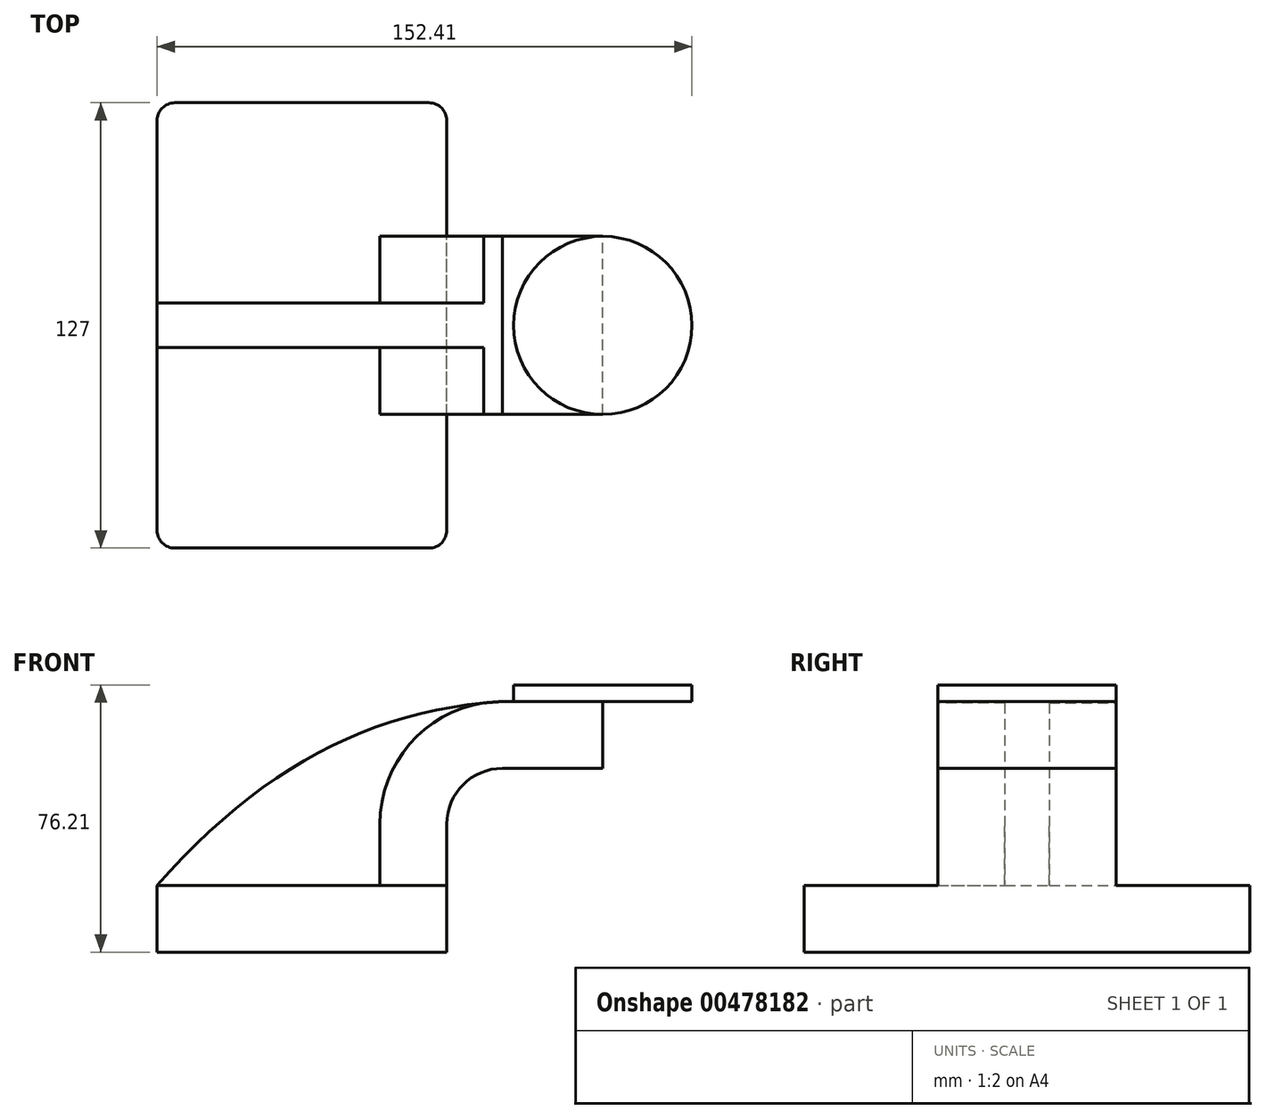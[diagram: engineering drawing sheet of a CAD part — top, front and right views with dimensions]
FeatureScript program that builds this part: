
annotation { "Feature Type Name" : "Feature", "Feature Type Description" : "" }
export const myFeature = defineFeature(function(context is Context, id is Id, definition is map)
    precondition{}
    {
        {
            var Q0;
            Q0=qCreatedBy(makeId("Front.planeOp"),FACE);
            var sketch = newSketch(context, id + "F0", { "sketchPlane" : qUnion([Q0])});
            skLineSegment(sketch, "E0.bottom", {"start": v(41.28, -9.52) * mm, "end": v(-41.27, -9.52) * mm});
            skLineSegment(sketch, "E0.top", {"start": v(41.27, 9.53) * mm, "end": v(-41.27, 9.53) * mm});
            skLineSegment(sketch, "E0.left", {"start": v(41.28, -9.52) * mm, "end": v(41.28, 9.53) * mm});
            skLineSegment(sketch, "E0.right", {"start": v(-41.27, -9.52) * mm, "end": v(-41.27, 9.53) * mm});
            skPoint(sketch, "E0.middle", {"position": v(0, 0) * mm});
            skLineSegment(sketch, "E1", {"start": v(41.27, 9.53) * mm, "end": v(41.27, 27) * mm});
            skArc(sketch, "E2", {"start": v(41.28, 27) * mm, "mid": v(45.92, 38.23) * mm, "end": v(57.15, 42.88) * mm});
            skLineSegment(sketch, "E3", {"start": v(57.15, 42.88) * mm, "end": v(85.72, 42.88) * mm});
            skLineSegment(sketch, "E4.bottom", {"start": v(111.12, 66.68) * mm, "end": v(60.32, 66.68) * mm});
            skLineSegment(sketch, "E4.top", {"start": v(111.12, 38.1) * mm, "end": v(60.32, 38.1) * mm});
            skLineSegment(sketch, "E4.left", {"start": v(111.12, 66.68) * mm, "end": v(111.12, 38.1) * mm});
            skLineSegment(sketch, "E4.right", {"start": v(60.32, 66.68) * mm, "end": v(60.32, 38.1) * mm});
            skPoint(sketch, "E4.middle", {"position": v(85.72, 52.39) * mm});
            skLineSegment(sketch, "E5", {"start": v(111.12, 66.68) * mm, "end": v(111.12, -9.67) * mm});
            skLineSegment(sketch, "E6.0", {"start": v(57.15, 61.93) * mm, "end": v(85.72, 61.93) * mm});
            skArc(sketch, "E6.1", {"start": v(22.23, 27) * mm, "mid": v(32.45, 51.7) * mm, "end": v(57.15, 61.93) * mm});
            skLineSegment(sketch, "E6.2", {"start": v(22.23, 9.53) * mm, "end": v(22.23, 27) * mm});
            skFitSpline(sketch, "E7", {"points": [v(57.15, 61.93) * mm, v(-41.28, 9.52) * mm], "startDerivative": vector(-112.77, -6.5) * mm, "endDerivative": vector(-88.55, -100.44) * mm});
            skLineSegment(sketch, "E8", {"start": v(85.72, 66.68) * mm, "end": v(85.72, 38.1) * mm});
            skSolve(sketch);
        }
        {
            var Q0;
            Q0=makeQuery(id+"F0.imprint","IMPRINT",FACE,{"disambiguationData":[TD([[makeQuery(id+"F0.imprint","IMPRINT",EDGE,{"derivedFrom":sQuery(id+"F0.wireOp",EDGE,"E0.bottom")}),-1.0]])]});
            extrude(context, id + "F1", {"entities" : qUnion([Q0]), "endBound" : BoundingType.SYMMETRIC, "depth" : 127 * mm});
        }
        {
            var Q0;
            {var subQ4=sQuery(id+"F0.wireOp",EDGE,"E1");Q0=makeQuery(id+"F0.imprint","IMPRINT",FACE,{"disambiguationData":[TD([[makeQuery(id+"F0.imprint","IMPRINT",EDGE,{"derivedFrom":subQ4}),1.0]])]});}
            var Q1;
            {var subQ0=sQuery(id+"F0.wireOp",EDGE,"E8");var subQ1=sQuery(id+"F0.wireOp",EDGE,"E3");var subQ2=makeQuery(id+"F0.imprint","INTERSECT",VERTEX,{"derivedFrom":[subQ1,subQ0]});Q1=makeQuery(id+"F0.imprint","IMPRINT",FACE,{"disambiguationData":[TD([[makeQuery(id+"F0.imprint","IMPRINT",EDGE,{"disambiguationData":[TD([[subQ2,1.0]])],"derivedFrom":subQ1}),1.0]])]});}
            extrude(context, id + "F2", {"entities" : qUnion([Q0, Q1]), "operationType" : NewBodyOperationType.ADD, "endBound" : BoundingType.SYMMETRIC, "depth" : 50.8 * mm});
        }
        {
            var Q0;
            {var subQ3=sQuery(id+"F0.wireOp",EDGE,"E6.2");Q0=makeQuery(id+"F0.imprint","IMPRINT",FACE,{"disambiguationData":[TD([[makeQuery(id+"F0.imprint","IMPRINT",EDGE,{"derivedFrom":subQ3}),1.0]])]});}
            extrude(context, id + "F3", {"entities" : qUnion([Q0]), "operationType" : NewBodyOperationType.ADD, "endBound" : BoundingType.SYMMETRIC, "depth" : 12.7 * mm});
        }
        {
            var Q0;
            {var subQ0=sQuery(id+"F0.wireOp",EDGE,"E5");var subQ1=sQuery(id+"F0.wireOp",EDGE,"E4.bottom");var subQ2=makeQuery(id+"F0.imprint","INTERSECT",VERTEX,{"derivedFrom":[subQ1,subQ0]});Q0=makeQuery(id+"F0.imprint","IMPRINT",FACE,{"disambiguationData":[TD([[makeQuery(id+"F0.imprint","IMPRINT",EDGE,{"disambiguationData":[TD([[subQ2,-1.0]])],"derivedFrom":subQ1}),1.0]])]});}
            var Q1;
            Q1=sQuery(id+"F0.wireOp",EDGE,"E8");
            revolve(context, id + "F4", {"operationType" : NewBodyOperationType.ADD, "entities" : qUnion([Q0]), "axis" : qUnion([Q1]), "revolveType" : RevolveType.FULL});
        }
        {
            var Q0;
            Q0=makeQuery(id+"F1.opExtrude","CAP_EDGE",EDGE,{"disambiguationData":[OSD([sQuery(id+"F0.wireOp",EDGE,"E0.right")])],"isStart":false});
            var Q1;
            Q1=makeQuery(id+"F1.opExtrude","CAP_EDGE",EDGE,{"disambiguationData":[OSD([sQuery(id+"F0.wireOp",EDGE,"E0.left")])],"isStart":false});
            var Q2;
            Q2=makeQuery(id+"F1.opExtrude","CAP_EDGE",EDGE,{"disambiguationData":[OSD([sQuery(id+"F0.wireOp",EDGE,"E0.left")])],"isStart":true});
            var Q3;
            Q3=makeQuery(id+"F1.opExtrude","CAP_EDGE",EDGE,{"disambiguationData":[OSD([sQuery(id+"F0.wireOp",EDGE,"E0.right")])],"isStart":true});
            fillet(context, id + "F5", {"entities" : qUnion([Q0, Q1, Q2, Q3]), "radius" : 5.08 * mm, "tangentPropagation" : true, "allowEdgeOverflow" : false});
        }
    });
